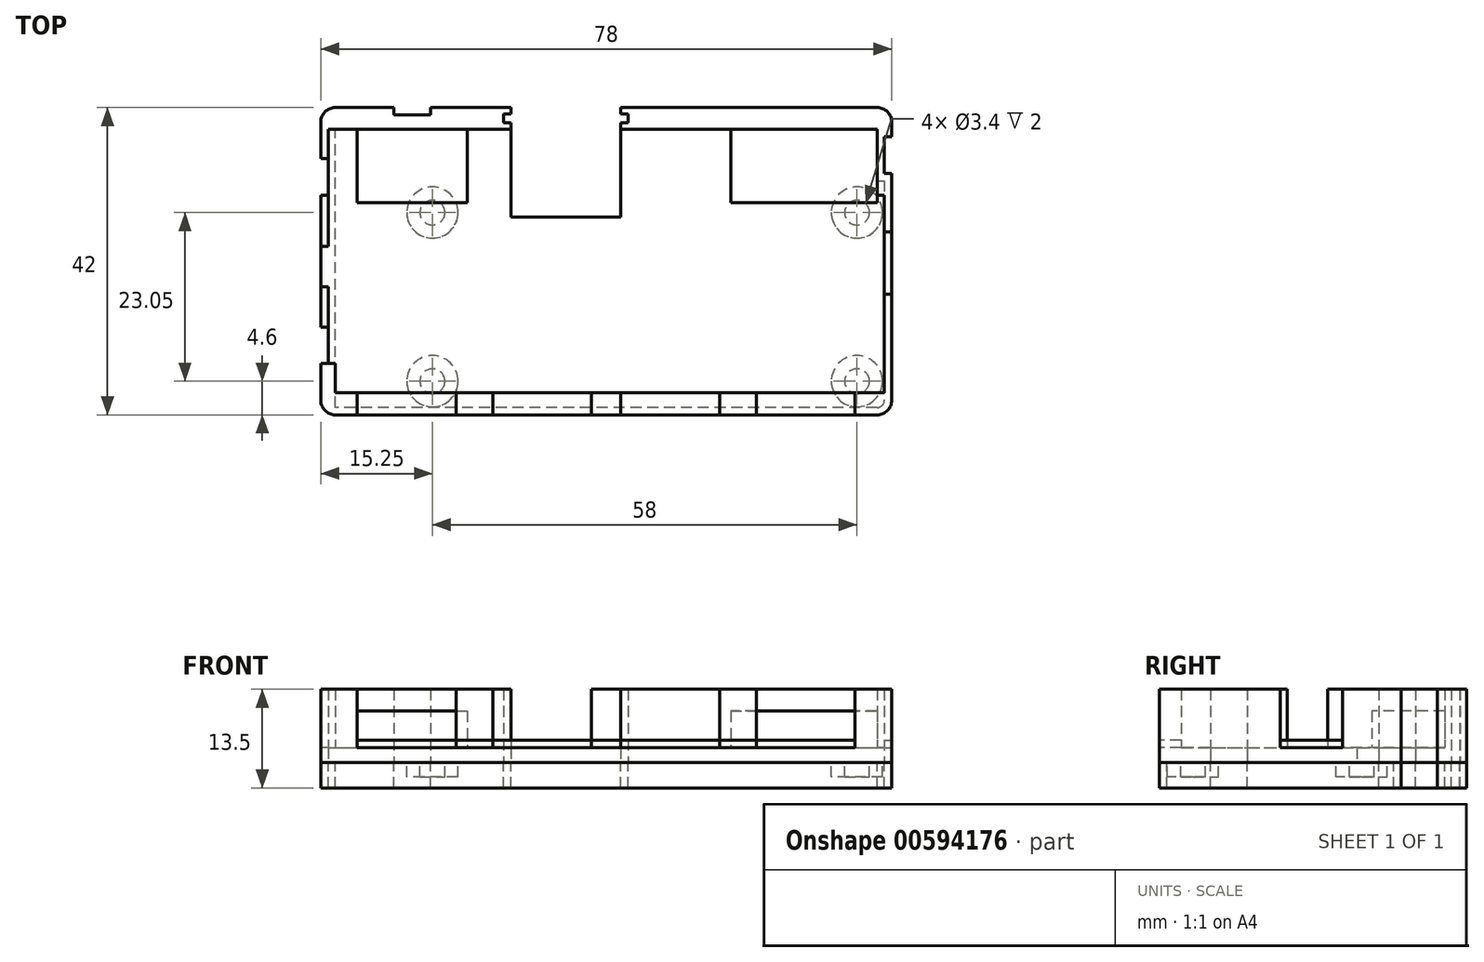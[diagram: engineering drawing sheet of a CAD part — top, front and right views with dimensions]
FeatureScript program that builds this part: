
annotation { "Feature Type Name" : "Feature", "Feature Type Description" : "" }
export const myFeature = defineFeature(function(context is Context, id is Id, definition is map)
    precondition{}
    {
        {
            var Q0;
            Q0=qCreatedBy(makeId("Top.planeOp"),FACE);
            var sketch = newSketch(context, id + "F0", { "sketchPlane" : qUnion([Q0])});
            skLineSegment(sketch, "E0", {"start": v(0, 0) * mm, "end": v(0, 7) * mm});
            skLineSegment(sketch, "E1", {"start": v(0, 7) * mm, "end": v(1, 7) * mm});
            skLineSegment(sketch, "E2", {"start": v(1, 7) * mm, "end": v(1, 12) * mm});
            skLineSegment(sketch, "E3", {"start": v(1, 12) * mm, "end": v(0, 12) * mm});
            skLineSegment(sketch, "E4", {"start": v(0, 12) * mm, "end": v(0, 30) * mm});
            skLineSegment(sketch, "E5", {"start": v(0, 30) * mm, "end": v(1, 30) * mm});
            skLineSegment(sketch, "E6", {"start": v(1, 30) * mm, "end": v(1, 35) * mm});
            skLineSegment(sketch, "E7", {"start": v(1, 35) * mm, "end": v(0, 35) * mm});
            skLineSegment(sketch, "E8", {"start": v(0, 35) * mm, "end": v(0, 42) * mm});
            skLineSegment(sketch, "E9", {"start": v(0, 42) * mm, "end": v(10, 42) * mm});
            skLineSegment(sketch, "E10", {"start": v(10, 42) * mm, "end": v(10, 41) * mm});
            skLineSegment(sketch, "E11", {"start": v(10, 41) * mm, "end": v(15, 41) * mm});
            skLineSegment(sketch, "E12", {"start": v(15, 41) * mm, "end": v(15, 42) * mm});
            skLineSegment(sketch, "E13", {"start": v(15, 42) * mm, "end": v(26, 42) * mm});
            skLineSegment(sketch, "E14", {"start": v(26, 42) * mm, "end": v(26, 41.1) * mm});
            skLineSegment(sketch, "E15", {"start": v(26, 41.1) * mm, "end": v(25, 41.1) * mm});
            skLineSegment(sketch, "E16", {"start": v(25, 41.1) * mm, "end": v(25, 39.9) * mm});
            skLineSegment(sketch, "E17", {"start": v(25, 39.9) * mm, "end": v(26, 39.9) * mm});
            skLineSegment(sketch, "E18", {"start": v(26, 39.9) * mm, "end": v(26, 27) * mm});
            skLineSegment(sketch, "E19", {"start": v(26, 27) * mm, "end": v(41, 27) * mm});
            skLineSegment(sketch, "E20", {"start": v(41, 27) * mm, "end": v(41, 39.9) * mm});
            skLineSegment(sketch, "E21", {"start": v(41, 39.9) * mm, "end": v(42, 39.9) * mm});
            skLineSegment(sketch, "E22", {"start": v(42, 39.9) * mm, "end": v(42, 41.1) * mm});
            skLineSegment(sketch, "E23", {"start": v(42, 41.1) * mm, "end": v(41, 41.1) * mm});
            skLineSegment(sketch, "E24", {"start": v(41, 41.1) * mm, "end": v(41, 42) * mm});
            skLineSegment(sketch, "E25", {"start": v(41, 42) * mm, "end": v(78, 42) * mm});
            skLineSegment(sketch, "E26", {"start": v(78, 42) * mm, "end": v(78, 38) * mm});
            skLineSegment(sketch, "E27", {"start": v(78, 38) * mm, "end": v(77, 38) * mm});
            skLineSegment(sketch, "E28", {"start": v(77, 38) * mm, "end": v(77, 33) * mm});
            skLineSegment(sketch, "E29", {"start": v(77, 33) * mm, "end": v(78, 33) * mm});
            skLineSegment(sketch, "E30", {"start": v(78, 33) * mm, "end": v(78, 0) * mm});
            skLineSegment(sketch, "E31", {"start": v(78, 0) * mm, "end": v(0, 0) * mm});
            skSolve(sketch);
        }
        {
            var Q0;
            Q0 = qSketchRegion(id + "F0", true);
            extrude(context, id + "F1", {"entities" : qUnion([Q0]), "depth" : 2 * mm, "offsetDistance" : 25 * mm});
        }
        {
            var Q0;
            Q0=makeQuery(id+"F1.opExtrude","CAP_FACE",FACE,{"disambiguationData":[OSD([sQuery(id+"F0.wireOp",EDGE,"E0"),sQuery(id+"F0.wireOp",EDGE,"E1"),sQuery(id+"F0.wireOp",EDGE,"E2"),sQuery(id+"F0.wireOp",EDGE,"E3"),sQuery(id+"F0.wireOp",EDGE,"E4"),sQuery(id+"F0.wireOp",EDGE,"E5"),sQuery(id+"F0.wireOp",EDGE,"E6"),sQuery(id+"F0.wireOp",EDGE,"E7"),sQuery(id+"F0.wireOp",EDGE,"E8"),sQuery(id+"F0.wireOp",EDGE,"E9"),sQuery(id+"F0.wireOp",EDGE,"E10"),sQuery(id+"F0.wireOp",EDGE,"E11"),sQuery(id+"F0.wireOp",EDGE,"E12"),sQuery(id+"F0.wireOp",EDGE,"E13"),sQuery(id+"F0.wireOp",EDGE,"E14"),sQuery(id+"F0.wireOp",EDGE,"E15"),sQuery(id+"F0.wireOp",EDGE,"E16"),sQuery(id+"F0.wireOp",EDGE,"E17"),sQuery(id+"F0.wireOp",EDGE,"E18"),sQuery(id+"F0.wireOp",EDGE,"E19"),sQuery(id+"F0.wireOp",EDGE,"E20"),sQuery(id+"F0.wireOp",EDGE,"E21"),sQuery(id+"F0.wireOp",EDGE,"E22"),sQuery(id+"F0.wireOp",EDGE,"E23"),sQuery(id+"F0.wireOp",EDGE,"E24"),sQuery(id+"F0.wireOp",EDGE,"E25"),sQuery(id+"F0.wireOp",EDGE,"E26"),sQuery(id+"F0.wireOp",EDGE,"E27"),sQuery(id+"F0.wireOp",EDGE,"E28"),sQuery(id+"F0.wireOp",EDGE,"E29"),sQuery(id+"F0.wireOp",EDGE,"E30"),sQuery(id+"F0.wireOp",EDGE,"E31")])],"isStart":false});
            var sketch = newSketch(context, id + "F2", { "sketchPlane" : qUnion([Q0])});
            skPoint(sketch, "E32.0", {"position": v(0, 0) * mm});
            skPoint(sketch, "E33.0", {"position": v(78, 0) * mm});
            skPoint(sketch, "E34.0", {"position": v(78, 42) * mm});
            skPoint(sketch, "E35.0", {"position": v(0, 42) * mm});
            skPoint(sketch, "E36.0", {"position": v(26, 42) * mm});
            skPoint(sketch, "E37.0", {"position": v(41, 42) * mm});
            skPoint(sketch, "E38.0", {"position": v(10, 42) * mm});
            skPoint(sketch, "E39.0", {"position": v(15, 42) * mm});
            skPoint(sketch, "E40.0", {"position": v(15, 41) * mm});
            skPoint(sketch, "E41.0", {"position": v(10, 41) * mm});
            skPoint(sketch, "E42.0", {"position": v(0, 35) * mm});
            skPoint(sketch, "E43.0", {"position": v(0, 7) * mm});
            skPoint(sketch, "E44.0", {"position": v(78, 38) * mm});
            skPoint(sketch, "E45.0", {"position": v(77, 38) * mm});
            skPoint(sketch, "E46.0", {"position": v(77, 33) * mm});
            skPoint(sketch, "E47.0", {"position": v(78, 33) * mm});
            skPoint(sketch, "E48.0", {"position": v(26, 41.1) * mm});
            skPoint(sketch, "E49.0", {"position": v(25, 41.1) * mm});
            skPoint(sketch, "E50.0", {"position": v(25, 39.9) * mm});
            skPoint(sketch, "E51.0", {"position": v(26, 39.9) * mm});
            skPoint(sketch, "E52.0", {"position": v(41, 41.1) * mm});
            skPoint(sketch, "E53.0", {"position": v(42, 41.1) * mm});
            skPoint(sketch, "E54.0", {"position": v(42, 39.9) * mm});
            skPoint(sketch, "E55.0", {"position": v(41, 39.9) * mm});
            skLineSegment(sketch, "E56", {"start": v(15, 42) * mm, "end": v(15, 41) * mm});
            skLineSegment(sketch, "E57", {"start": v(15, 41) * mm, "end": v(10, 41) * mm});
            skLineSegment(sketch, "E58", {"start": v(10, 42) * mm, "end": v(10, 41) * mm});
            skLineSegment(sketch, "E59", {"start": v(10, 42) * mm, "end": v(0, 42) * mm});
            skLineSegment(sketch, "E60", {"start": v(0, 42) * mm, "end": v(0, 35) * mm});
            skLineSegment(sketch, "E61", {"start": v(0, 35) * mm, "end": v(1, 35) * mm});
            skLineSegment(sketch, "E62", {"start": v(1, 35) * mm, "end": v(1, 39) * mm});
            skLineSegment(sketch, "E63", {"start": v(1, 39) * mm, "end": v(26, 39) * mm});
            skLineSegment(sketch, "E64", {"start": v(26, 39) * mm, "end": v(26, 39.9) * mm});
            skLineSegment(sketch, "E65", {"start": v(25, 39.9) * mm, "end": v(25, 41.1) * mm});
            skLineSegment(sketch, "E66", {"start": v(26, 41.1) * mm, "end": v(26, 42) * mm});
            skLineSegment(sketch, "E67", {"start": v(25, 41.1) * mm, "end": v(26, 41.1) * mm});
            skLineSegment(sketch, "E68", {"start": v(25, 39.9) * mm, "end": v(26, 39.9) * mm});
            skLineSegment(sketch, "E69", {"start": v(0, 30) * mm, "end": v(1, 30) * mm});
            skLineSegment(sketch, "E70", {"start": v(1, 30) * mm, "end": v(1, 23) * mm});
            skLineSegment(sketch, "E71", {"start": v(1, 23) * mm, "end": v(0, 23) * mm});
            skLineSegment(sketch, "E72", {"start": v(0, 23) * mm, "end": v(0, 30) * mm});
            skLineSegment(sketch, "E73", {"start": v(0, 12) * mm, "end": v(1, 12) * mm});
            skLineSegment(sketch, "E74", {"start": v(1, 12) * mm, "end": v(1, 17.5) * mm});
            skLineSegment(sketch, "E75", {"start": v(1, 17.5) * mm, "end": v(0, 17.5) * mm});
            skLineSegment(sketch, "E76", {"start": v(0, 17.5) * mm, "end": v(0, 12) * mm});
            skLineSegment(sketch, "E77", {"start": v(0, 7) * mm, "end": v(2, 7) * mm});
            skLineSegment(sketch, "E78", {"start": v(2, 7) * mm, "end": v(2, 3) * mm});
            skLineSegment(sketch, "E79", {"start": v(2, 3) * mm, "end": v(5, 3) * mm});
            skLineSegment(sketch, "E80", {"start": v(5, 3) * mm, "end": v(5, 0) * mm});
            skLineSegment(sketch, "E81", {"start": v(5, 0) * mm, "end": v(0, 0) * mm});
            skLineSegment(sketch, "E82", {"start": v(0, 7) * mm, "end": v(0, 0) * mm});
            skLineSegment(sketch, "E83", {"start": v(41, 39) * mm, "end": v(41, 39.9) * mm});
            skLineSegment(sketch, "E84", {"start": v(42, 39.9) * mm, "end": v(42, 41.1) * mm});
            skLineSegment(sketch, "E85", {"start": v(41, 41.1) * mm, "end": v(42, 41.1) * mm});
            skLineSegment(sketch, "E86", {"start": v(42, 39.9) * mm, "end": v(41, 39.9) * mm});
            skLineSegment(sketch, "E87", {"start": v(41, 41.1) * mm, "end": v(41, 42) * mm});
            skLineSegment(sketch, "E88", {"start": v(78, 42) * mm, "end": v(41, 42) * mm});
            skLineSegment(sketch, "E89", {"start": v(78, 42) * mm, "end": v(78, 38) * mm});
            skLineSegment(sketch, "E90", {"start": v(78, 38) * mm, "end": v(77, 38) * mm});
            skLineSegment(sketch, "E91", {"start": v(77, 38) * mm, "end": v(77, 33) * mm});
            skLineSegment(sketch, "E92", {"start": v(77, 33) * mm, "end": v(78, 33) * mm});
            skLineSegment(sketch, "E93", {"start": v(78, 33) * mm, "end": v(78, 25) * mm});
            skLineSegment(sketch, "E94", {"start": v(78, 25) * mm, "end": v(77, 25) * mm});
            skLineSegment(sketch, "E95", {"start": v(77, 25) * mm, "end": v(77, 30) * mm});
            skLineSegment(sketch, "E96", {"start": v(77, 30) * mm, "end": v(76, 30) * mm});
            skLineSegment(sketch, "E97", {"start": v(76, 30) * mm, "end": v(76, 39) * mm});
            skLineSegment(sketch, "E98", {"start": v(41, 39) * mm, "end": v(76, 39) * mm});
            skLineSegment(sketch, "E99", {"start": v(78, 16.5) * mm, "end": v(78, 0) * mm});
            skLineSegment(sketch, "E100", {"start": v(78, 0) * mm, "end": v(73, 0) * mm});
            skLineSegment(sketch, "E101", {"start": v(73, 0) * mm, "end": v(73, 3) * mm});
            skLineSegment(sketch, "E102", {"start": v(73, 3) * mm, "end": v(77, 3) * mm});
            skLineSegment(sketch, "E103", {"start": v(77, 3) * mm, "end": v(77, 16.5) * mm});
            skLineSegment(sketch, "E104", {"start": v(77, 16.5) * mm, "end": v(78, 16.5) * mm});
            skLineSegment(sketch, "E105.bottom", {"start": v(18.5, 0) * mm, "end": v(23.5, 0) * mm});
            skLineSegment(sketch, "E105.top", {"start": v(18.5, 3) * mm, "end": v(23.5, 3) * mm});
            skLineSegment(sketch, "E105.left", {"start": v(18.5, 0) * mm, "end": v(18.5, 3) * mm});
            skLineSegment(sketch, "E105.right", {"start": v(23.5, 0) * mm, "end": v(23.5, 3) * mm});
            skLineSegment(sketch, "E106.bottom", {"start": v(37, 3) * mm, "end": v(41, 3) * mm});
            skLineSegment(sketch, "E106.top", {"start": v(37, 0) * mm, "end": v(41, 0) * mm});
            skLineSegment(sketch, "E106.left", {"start": v(37, 3) * mm, "end": v(37, 0) * mm});
            skLineSegment(sketch, "E106.right", {"start": v(41, 3) * mm, "end": v(41, 0) * mm});
            skLineSegment(sketch, "E107.bottom", {"start": v(54.5, 3) * mm, "end": v(59.5, 3) * mm});
            skLineSegment(sketch, "E107.top", {"start": v(54.5, 0) * mm, "end": v(59.5, 0) * mm});
            skLineSegment(sketch, "E107.left", {"start": v(54.5, 3) * mm, "end": v(54.5, 0) * mm});
            skLineSegment(sketch, "E107.right", {"start": v(59.5, 3) * mm, "end": v(59.5, 0) * mm});
            skLineSegment(sketch, "E108", {"start": v(15, 42) * mm, "end": v(26, 42) * mm});
            skSolve(sketch);
        }
        {
            var Q0;
            Q0 = qSketchRegion(id + "F2", true);
            extrude(context, id + "F3", {"entities" : qUnion([Q0]), "operationType" : NewBodyOperationType.ADD, "depth" : 8 * mm, "offsetDistance" : 25 * mm});
        }
        {
            var Q0;
            Q0=makeQuery(id+"F1.opExtrude","CAP_FACE",FACE,{"disambiguationData":[OSD([sQuery(id+"F0.wireOp",EDGE,"E0"),sQuery(id+"F0.wireOp",EDGE,"E1"),sQuery(id+"F0.wireOp",EDGE,"E2"),sQuery(id+"F0.wireOp",EDGE,"E3"),sQuery(id+"F0.wireOp",EDGE,"E4"),sQuery(id+"F0.wireOp",EDGE,"E5"),sQuery(id+"F0.wireOp",EDGE,"E6"),sQuery(id+"F0.wireOp",EDGE,"E7"),sQuery(id+"F0.wireOp",EDGE,"E8"),sQuery(id+"F0.wireOp",EDGE,"E9"),sQuery(id+"F0.wireOp",EDGE,"E10"),sQuery(id+"F0.wireOp",EDGE,"E11"),sQuery(id+"F0.wireOp",EDGE,"E12"),sQuery(id+"F0.wireOp",EDGE,"E13"),sQuery(id+"F0.wireOp",EDGE,"E14"),sQuery(id+"F0.wireOp",EDGE,"E15"),sQuery(id+"F0.wireOp",EDGE,"E16"),sQuery(id+"F0.wireOp",EDGE,"E17"),sQuery(id+"F0.wireOp",EDGE,"E18"),sQuery(id+"F0.wireOp",EDGE,"E19"),sQuery(id+"F0.wireOp",EDGE,"E20"),sQuery(id+"F0.wireOp",EDGE,"E21"),sQuery(id+"F0.wireOp",EDGE,"E22"),sQuery(id+"F0.wireOp",EDGE,"E23"),sQuery(id+"F0.wireOp",EDGE,"E24"),sQuery(id+"F0.wireOp",EDGE,"E25"),sQuery(id+"F0.wireOp",EDGE,"E26"),sQuery(id+"F0.wireOp",EDGE,"E27"),sQuery(id+"F0.wireOp",EDGE,"E28"),sQuery(id+"F0.wireOp",EDGE,"E29"),sQuery(id+"F0.wireOp",EDGE,"E30"),sQuery(id+"F0.wireOp",EDGE,"E31")])],"isStart":false});
            var sketch = newSketch(context, id + "F4", { "sketchPlane" : qUnion([Q0])});
            skPoint(sketch, "E109.0", {"position": v(5, 0) * mm});
            skPoint(sketch, "E110.0", {"position": v(73, 3) * mm});
            skPoint(sketch, "E111.0", {"position": v(78, 16.5) * mm});
            skPoint(sketch, "E112.0", {"position": v(77, 25) * mm});
            skLineSegment(sketch, "E113.bottom", {"start": v(5, 0) * mm, "end": v(73, 0) * mm});
            skLineSegment(sketch, "E113.top", {"start": v(5, 3) * mm, "end": v(73, 3) * mm});
            skLineSegment(sketch, "E113.left", {"start": v(5, 0) * mm, "end": v(5, 3) * mm});
            skLineSegment(sketch, "E113.right", {"start": v(73, 0) * mm, "end": v(73, 3) * mm});
            skLineSegment(sketch, "E114.bottom", {"start": v(78, 16.5) * mm, "end": v(77, 16.5) * mm});
            skLineSegment(sketch, "E114.top", {"start": v(78, 25) * mm, "end": v(77, 25) * mm});
            skLineSegment(sketch, "E114.left", {"start": v(78, 16.5) * mm, "end": v(78, 25) * mm});
            skLineSegment(sketch, "E114.right", {"start": v(77, 16.5) * mm, "end": v(77, 25) * mm});
            skSolve(sketch);
        }
        {
            var Q0;
            Q0 = qSketchRegion(id + "F4", true);
            extrude(context, id + "F5", {"entities" : qUnion([Q0]), "depth" : 1 * mm, "offsetDistance" : 25 * mm});
        }
        {
            var Q0;
            Q0=makeQuery(id+"F1.opExtrude","CAP_FACE",FACE,{"disambiguationData":[OSD([sQuery(id+"F0.wireOp",EDGE,"E0"),sQuery(id+"F0.wireOp",EDGE,"E1"),sQuery(id+"F0.wireOp",EDGE,"E2"),sQuery(id+"F0.wireOp",EDGE,"E3"),sQuery(id+"F0.wireOp",EDGE,"E4"),sQuery(id+"F0.wireOp",EDGE,"E5"),sQuery(id+"F0.wireOp",EDGE,"E6"),sQuery(id+"F0.wireOp",EDGE,"E7"),sQuery(id+"F0.wireOp",EDGE,"E8"),sQuery(id+"F0.wireOp",EDGE,"E9"),sQuery(id+"F0.wireOp",EDGE,"E10"),sQuery(id+"F0.wireOp",EDGE,"E11"),sQuery(id+"F0.wireOp",EDGE,"E12"),sQuery(id+"F0.wireOp",EDGE,"E13"),sQuery(id+"F0.wireOp",EDGE,"E14"),sQuery(id+"F0.wireOp",EDGE,"E15"),sQuery(id+"F0.wireOp",EDGE,"E16"),sQuery(id+"F0.wireOp",EDGE,"E17"),sQuery(id+"F0.wireOp",EDGE,"E18"),sQuery(id+"F0.wireOp",EDGE,"E19"),sQuery(id+"F0.wireOp",EDGE,"E20"),sQuery(id+"F0.wireOp",EDGE,"E21"),sQuery(id+"F0.wireOp",EDGE,"E22"),sQuery(id+"F0.wireOp",EDGE,"E23"),sQuery(id+"F0.wireOp",EDGE,"E24"),sQuery(id+"F0.wireOp",EDGE,"E25"),sQuery(id+"F0.wireOp",EDGE,"E26"),sQuery(id+"F0.wireOp",EDGE,"E27"),sQuery(id+"F0.wireOp",EDGE,"E28"),sQuery(id+"F0.wireOp",EDGE,"E29"),sQuery(id+"F0.wireOp",EDGE,"E30"),sQuery(id+"F0.wireOp",EDGE,"E31")])],"isStart":false});
            var sketch = newSketch(context, id + "F6", { "sketchPlane" : qUnion([Q0])});
            skPoint(sketch, "E115.0", {"position": v(1, 39) * mm});
            skPoint(sketch, "E116.0", {"position": v(76, 39) * mm});
            skLineSegment(sketch, "E117.bottom", {"start": v(5, 39) * mm, "end": v(20, 39) * mm});
            skLineSegment(sketch, "E117.top", {"start": v(5, 29) * mm, "end": v(20, 29) * mm});
            skLineSegment(sketch, "E117.left", {"start": v(5, 39) * mm, "end": v(5, 29) * mm});
            skLineSegment(sketch, "E117.right", {"start": v(20, 39) * mm, "end": v(20, 29) * mm});
            skLineSegment(sketch, "E118.bottom", {"start": v(76, 39) * mm, "end": v(56, 39) * mm});
            skLineSegment(sketch, "E118.top", {"start": v(76, 29) * mm, "end": v(56, 29) * mm});
            skLineSegment(sketch, "E118.left", {"start": v(76, 39) * mm, "end": v(76, 29) * mm});
            skLineSegment(sketch, "E118.right", {"start": v(56, 39) * mm, "end": v(56, 29) * mm});
            skSolve(sketch);
        }
        {
            var Q0;
            Q0 = qSketchRegion(id + "F6", true);
            extrude(context, id + "F7", {"entities" : qUnion([Q0]), "depth" : 5 * mm, "offsetDistance" : 25 * mm});
        }
        {
            var Q0;
            Q0=makeQuery(id+"F1.opExtrude","CAP_FACE",FACE,{"disambiguationData":[OSD([sQuery(id+"F0.wireOp",EDGE,"E0"),sQuery(id+"F0.wireOp",EDGE,"E1"),sQuery(id+"F0.wireOp",EDGE,"E2"),sQuery(id+"F0.wireOp",EDGE,"E3"),sQuery(id+"F0.wireOp",EDGE,"E4"),sQuery(id+"F0.wireOp",EDGE,"E5"),sQuery(id+"F0.wireOp",EDGE,"E6"),sQuery(id+"F0.wireOp",EDGE,"E7"),sQuery(id+"F0.wireOp",EDGE,"E8"),sQuery(id+"F0.wireOp",EDGE,"E9"),sQuery(id+"F0.wireOp",EDGE,"E10"),sQuery(id+"F0.wireOp",EDGE,"E11"),sQuery(id+"F0.wireOp",EDGE,"E12"),sQuery(id+"F0.wireOp",EDGE,"E13"),sQuery(id+"F0.wireOp",EDGE,"E14"),sQuery(id+"F0.wireOp",EDGE,"E15"),sQuery(id+"F0.wireOp",EDGE,"E16"),sQuery(id+"F0.wireOp",EDGE,"E17"),sQuery(id+"F0.wireOp",EDGE,"E18"),sQuery(id+"F0.wireOp",EDGE,"E19"),sQuery(id+"F0.wireOp",EDGE,"E20"),sQuery(id+"F0.wireOp",EDGE,"E21"),sQuery(id+"F0.wireOp",EDGE,"E22"),sQuery(id+"F0.wireOp",EDGE,"E23"),sQuery(id+"F0.wireOp",EDGE,"E24"),sQuery(id+"F0.wireOp",EDGE,"E25"),sQuery(id+"F0.wireOp",EDGE,"E26"),sQuery(id+"F0.wireOp",EDGE,"E27"),sQuery(id+"F0.wireOp",EDGE,"E28"),sQuery(id+"F0.wireOp",EDGE,"E29"),sQuery(id+"F0.wireOp",EDGE,"E30"),sQuery(id+"F0.wireOp",EDGE,"E31")])],"isStart":true});
            var sketch = newSketch(context, id + "F8", { "sketchPlane" : qUnion([Q0])});
            skPoint(sketch, "E119.0", {"position": v(0, 0) * mm});
            skPoint(sketch, "E120.0", {"position": v(1, -7) * mm});
            skPoint(sketch, "E121.0", {"position": v(0, -7) * mm});
            skPoint(sketch, "E122.0", {"position": v(1, -12) * mm});
            skPoint(sketch, "E123.0", {"position": v(0, -12) * mm});
            skPoint(sketch, "E124.0", {"position": v(0, -30) * mm});
            skPoint(sketch, "E125.0", {"position": v(1, -30) * mm});
            skPoint(sketch, "E126.0", {"position": v(1, -35) * mm});
            skPoint(sketch, "E127.0", {"position": v(0, -35) * mm});
            skPoint(sketch, "E128.0", {"position": v(0, -42) * mm});
            skPoint(sketch, "E129.0", {"position": v(10, -42) * mm});
            skPoint(sketch, "E130.0", {"position": v(10, -41) * mm});
            skPoint(sketch, "E131.0", {"position": v(15, -41) * mm});
            skPoint(sketch, "E132.0", {"position": v(15, -42) * mm});
            skPoint(sketch, "E133.0", {"position": v(26, -42) * mm});
            skPoint(sketch, "E134.0", {"position": v(26, -41.1) * mm});
            skPoint(sketch, "E135.0", {"position": v(25, -41.1) * mm});
            skPoint(sketch, "E136.0", {"position": v(25, -39.9) * mm});
            skPoint(sketch, "E137.0", {"position": v(26, -39.9) * mm});
            skPoint(sketch, "E138.0", {"position": v(41, -39.9) * mm});
            skPoint(sketch, "E139.0", {"position": v(42, -39.9) * mm});
            skPoint(sketch, "E140.0", {"position": v(42, -41.1) * mm});
            skPoint(sketch, "E141.0", {"position": v(41, -41.1) * mm});
            skPoint(sketch, "E142.0", {"position": v(41, -42) * mm});
            skPoint(sketch, "E143.0", {"position": v(78, -42) * mm});
            skPoint(sketch, "E144.0", {"position": v(78, -38) * mm});
            skPoint(sketch, "E145.0", {"position": v(77, -38) * mm});
            skPoint(sketch, "E146.0", {"position": v(77, -33) * mm});
            skPoint(sketch, "E147.0", {"position": v(78, -33) * mm});
            skPoint(sketch, "E148.0", {"position": v(78, 0) * mm});
            skLineSegment(sketch, "E149", {"start": v(0, 0) * mm, "end": v(78, 0) * mm});
            skLineSegment(sketch, "E150", {"start": v(78, 0) * mm, "end": v(78, -33) * mm});
            skLineSegment(sketch, "E151", {"start": v(78, -33) * mm, "end": v(77, -33) * mm});
            skLineSegment(sketch, "E152", {"start": v(77, -33) * mm, "end": v(77, -38) * mm});
            skLineSegment(sketch, "E153", {"start": v(77, -38) * mm, "end": v(78, -38) * mm});
            skLineSegment(sketch, "E154", {"start": v(78, -38) * mm, "end": v(78, -42) * mm});
            skLineSegment(sketch, "E155", {"start": v(78, -42) * mm, "end": v(41, -42) * mm});
            skLineSegment(sketch, "E156", {"start": v(41, -42) * mm, "end": v(41, -41.1) * mm});
            skLineSegment(sketch, "E157", {"start": v(41, -41.1) * mm, "end": v(42, -41.1) * mm});
            skLineSegment(sketch, "E158", {"start": v(41, -39.9) * mm, "end": v(41, -39) * mm});
            skLineSegment(sketch, "E159", {"start": v(41, -39) * mm, "end": v(76, -39) * mm});
            skLineSegment(sketch, "E160", {"start": v(76, -39) * mm, "end": v(76, -32) * mm});
            skLineSegment(sketch, "E161", {"start": v(76, -32) * mm, "end": v(77, -32) * mm});
            skLineSegment(sketch, "E162", {"start": v(77, -32) * mm, "end": v(77, -1) * mm});
            skLineSegment(sketch, "E163", {"start": v(77, -1) * mm, "end": v(2, -1) * mm});
            skLineSegment(sketch, "E164", {"start": v(2, -1) * mm, "end": v(2, -39) * mm});
            skLineSegment(sketch, "E165", {"start": v(2, -39) * mm, "end": v(26, -39) * mm});
            skLineSegment(sketch, "E166", {"start": v(26, -39) * mm, "end": v(26, -39.9) * mm});
            skLineSegment(sketch, "E167", {"start": v(26, -39.9) * mm, "end": v(25, -39.9) * mm});
            skLineSegment(sketch, "E168", {"start": v(25, -39.9) * mm, "end": v(25, -41.1) * mm});
            skLineSegment(sketch, "E169", {"start": v(25, -41.1) * mm, "end": v(26, -41.1) * mm});
            skLineSegment(sketch, "E170", {"start": v(26, -41.1) * mm, "end": v(26, -42) * mm});
            skLineSegment(sketch, "E171", {"start": v(26, -42) * mm, "end": v(15, -42) * mm});
            skLineSegment(sketch, "E172", {"start": v(15, -42) * mm, "end": v(15, -41) * mm});
            skLineSegment(sketch, "E173", {"start": v(15, -41) * mm, "end": v(10, -41) * mm});
            skLineSegment(sketch, "E174", {"start": v(10, -42) * mm, "end": v(10, -41) * mm});
            skLineSegment(sketch, "E175", {"start": v(10, -42) * mm, "end": v(0, -42) * mm});
            skLineSegment(sketch, "E176", {"start": v(0, -42) * mm, "end": v(0, -35) * mm});
            skLineSegment(sketch, "E177", {"start": v(0, -35) * mm, "end": v(1, -35) * mm});
            skLineSegment(sketch, "E178", {"start": v(1, -35) * mm, "end": v(1, -30) * mm});
            skLineSegment(sketch, "E179", {"start": v(1, -30) * mm, "end": v(0, -30) * mm});
            skLineSegment(sketch, "E180", {"start": v(0, -30) * mm, "end": v(0, -12) * mm});
            skLineSegment(sketch, "E181", {"start": v(0, -12) * mm, "end": v(1, -12) * mm});
            skLineSegment(sketch, "E182", {"start": v(1, -12) * mm, "end": v(1, -7) * mm});
            skLineSegment(sketch, "E183", {"start": v(1, -7) * mm, "end": v(0, -7) * mm});
            skLineSegment(sketch, "E184", {"start": v(0, -7) * mm, "end": v(0, 0) * mm});
            skLineSegment(sketch, "E185", {"start": v(42, -39.9) * mm, "end": v(41, -39.9) * mm});
            skLineSegment(sketch, "E186", {"start": v(42, -39.9) * mm, "end": v(42, -41.1) * mm});
            skSolve(sketch);
        }
        {
            var Q0;
            Q0 = qSketchRegion(id + "F8", true);
            extrude(context, id + "F9", {"entities" : qUnion([Q0]), "depth" : 3.5 * mm, "offsetDistance" : 25 * mm});
        }
        {
            var Q0;
            Q0=makeQuery(id+"F1.opExtrude","CAP_FACE",FACE,{"disambiguationData":[OSD([sQuery(id+"F0.wireOp",EDGE,"E0"),sQuery(id+"F0.wireOp",EDGE,"E1"),sQuery(id+"F0.wireOp",EDGE,"E2"),sQuery(id+"F0.wireOp",EDGE,"E3"),sQuery(id+"F0.wireOp",EDGE,"E4"),sQuery(id+"F0.wireOp",EDGE,"E5"),sQuery(id+"F0.wireOp",EDGE,"E6"),sQuery(id+"F0.wireOp",EDGE,"E7"),sQuery(id+"F0.wireOp",EDGE,"E8"),sQuery(id+"F0.wireOp",EDGE,"E9"),sQuery(id+"F0.wireOp",EDGE,"E10"),sQuery(id+"F0.wireOp",EDGE,"E11"),sQuery(id+"F0.wireOp",EDGE,"E12"),sQuery(id+"F0.wireOp",EDGE,"E13"),sQuery(id+"F0.wireOp",EDGE,"E14"),sQuery(id+"F0.wireOp",EDGE,"E15"),sQuery(id+"F0.wireOp",EDGE,"E16"),sQuery(id+"F0.wireOp",EDGE,"E17"),sQuery(id+"F0.wireOp",EDGE,"E18"),sQuery(id+"F0.wireOp",EDGE,"E19"),sQuery(id+"F0.wireOp",EDGE,"E20"),sQuery(id+"F0.wireOp",EDGE,"E21"),sQuery(id+"F0.wireOp",EDGE,"E22"),sQuery(id+"F0.wireOp",EDGE,"E23"),sQuery(id+"F0.wireOp",EDGE,"E24"),sQuery(id+"F0.wireOp",EDGE,"E25"),sQuery(id+"F0.wireOp",EDGE,"E26"),sQuery(id+"F0.wireOp",EDGE,"E27"),sQuery(id+"F0.wireOp",EDGE,"E28"),sQuery(id+"F0.wireOp",EDGE,"E29"),sQuery(id+"F0.wireOp",EDGE,"E30"),sQuery(id+"F0.wireOp",EDGE,"E31")])],"isStart":true});
            var sketch = newSketch(context, id + "F10", { "sketchPlane" : qUnion([Q0])});
            skPoint(sketch, "E187.0", {"position": v(78, 0) * mm});
            skCircle(sketch, "E188", {"center": v(73.25, -4.6) * mm, "radius": 3.5 * mm});
            skCircle(sketch, "E189", {"center": v(73.25, -4.6) * mm, "radius": 1.7 * mm});
            skCircle(sketch, "E190.0.1.0", {"center": v(73.25, -27.65) * mm, "radius": 1.7 * mm});
            skCircle(sketch, "E190.0.1.1", {"center": v(73.25, -27.65) * mm, "radius": 3.5 * mm});
            skCircle(sketch, "E190.1.0.0", {"center": v(15.25, -4.6) * mm, "radius": 1.7 * mm});
            skCircle(sketch, "E190.1.0.1", {"center": v(15.25, -4.6) * mm, "radius": 3.5 * mm});
            skCircle(sketch, "E190.1.1.0", {"center": v(15.25, -27.65) * mm, "radius": 1.7 * mm});
            skCircle(sketch, "E190.1.1.1", {"center": v(15.25, -27.65) * mm, "radius": 3.5 * mm});
            skLineSegment(sketch, "E190.direction1", {"start": v(73.25, -4.6) * mm, "end": v(15.25, -4.6) * mm, "construction": true});
            skLineSegment(sketch, "E190.direction2", {"start": v(73.25, -4.6) * mm, "end": v(73.25, -27.65) * mm, "construction": true});
            skSolve(sketch);
        }
        {
            var Q0;
            Q0 = qSketchRegion(id + "F10", true);
            extrude(context, id + "F11", {"entities" : qUnion([Q0]), "operationType" : NewBodyOperationType.ADD, "depth" : 2 * mm, "offsetDistance" : 25 * mm});
        }
        {
            var Q0;
            Q0=makeQuery(id+"F5.opExtrude","SWEPT_BODY",BODY,{"disambiguationData":[OSD([sQuery(id+"F4.wireOp",EDGE,"E114.bottom"),sQuery(id+"F4.wireOp",EDGE,"E114.top"),sQuery(id+"F4.wireOp",EDGE,"E114.left"),sQuery(id+"F4.wireOp",EDGE,"E114.right")])]});
            var Q1;
            Q1=makeQuery(id+"F9.opExtrude","SWEPT_BODY",BODY,{"disambiguationData":[OSD([sQuery(id+"F8.wireOp",EDGE,"E149"),sQuery(id+"F8.wireOp",EDGE,"E150"),sQuery(id+"F8.wireOp",EDGE,"E151"),sQuery(id+"F8.wireOp",EDGE,"E152"),sQuery(id+"F8.wireOp",EDGE,"E153"),sQuery(id+"F8.wireOp",EDGE,"E154"),sQuery(id+"F8.wireOp",EDGE,"E155"),sQuery(id+"F8.wireOp",EDGE,"E156"),sQuery(id+"F8.wireOp",EDGE,"E157"),sQuery(id+"F8.wireOp",EDGE,"E158"),sQuery(id+"F8.wireOp",EDGE,"E159"),sQuery(id+"F8.wireOp",EDGE,"E160"),sQuery(id+"F8.wireOp",EDGE,"E161"),sQuery(id+"F8.wireOp",EDGE,"E162"),sQuery(id+"F8.wireOp",EDGE,"E163"),sQuery(id+"F8.wireOp",EDGE,"E164"),sQuery(id+"F8.wireOp",EDGE,"E165"),sQuery(id+"F8.wireOp",EDGE,"E166"),sQuery(id+"F8.wireOp",EDGE,"E167"),sQuery(id+"F8.wireOp",EDGE,"E168"),sQuery(id+"F8.wireOp",EDGE,"E169"),sQuery(id+"F8.wireOp",EDGE,"E170"),sQuery(id+"F8.wireOp",EDGE,"E171"),sQuery(id+"F8.wireOp",EDGE,"E172"),sQuery(id+"F8.wireOp",EDGE,"E173"),sQuery(id+"F8.wireOp",EDGE,"E174"),sQuery(id+"F8.wireOp",EDGE,"E175"),sQuery(id+"F8.wireOp",EDGE,"E176"),sQuery(id+"F8.wireOp",EDGE,"E177"),sQuery(id+"F8.wireOp",EDGE,"E178"),sQuery(id+"F8.wireOp",EDGE,"E179"),sQuery(id+"F8.wireOp",EDGE,"E180"),sQuery(id+"F8.wireOp",EDGE,"E181"),sQuery(id+"F8.wireOp",EDGE,"E182"),sQuery(id+"F8.wireOp",EDGE,"E183"),sQuery(id+"F8.wireOp",EDGE,"E184"),sQuery(id+"F8.wireOp",EDGE,"E185"),sQuery(id+"F8.wireOp",EDGE,"E186")])]});
            booleanBodies(context, id + "F12", {"operationType" : BooleanOperationType.UNION, "tools" : qUnion([Q0, Q1])});
        }
        {
            var Q0;
            Q0=makeQuery(id+"F12.opBoolean","MERGE",EDGE,{"derivedFrom":[makeQuery(id+"F3.boolean.opBoolean","MERGE",EDGE,{"derivedFrom":[makeQuery(id+"F1.opExtrude","SWEPT_EDGE",EDGE,{"disambiguationData":[OSD([sQuery(id+"F0.wireOp",EDGE,"E30"),sQuery(id+"F0.wireOp",EDGE,"E31")])]}),makeQuery(id+"F3.opExtrude","SWEPT_EDGE",EDGE,{"disambiguationData":[OSD([sQuery(id+"F2.wireOp",EDGE,"E99"),sQuery(id+"F2.wireOp",EDGE,"E100")])]})]}),makeQuery(id+"F9.opExtrude","SWEPT_EDGE",EDGE,{"disambiguationData":[OSD([sQuery(id+"F8.wireOp",EDGE,"E149"),sQuery(id+"F8.wireOp",EDGE,"E150")])]})]});
            var Q1;
            Q1=makeQuery(id+"F12.opBoolean","MERGE",EDGE,{"derivedFrom":[makeQuery(id+"F3.boolean.opBoolean","MERGE",EDGE,{"derivedFrom":[makeQuery(id+"F1.opExtrude","SWEPT_EDGE",EDGE,{"disambiguationData":[OSD([sQuery(id+"F0.wireOp",EDGE,"E25"),sQuery(id+"F0.wireOp",EDGE,"E26")])]}),makeQuery(id+"F3.opExtrude","SWEPT_EDGE",EDGE,{"disambiguationData":[OSD([sQuery(id+"F2.wireOp",EDGE,"E88"),sQuery(id+"F2.wireOp",EDGE,"E89")])]})]}),makeQuery(id+"F9.opExtrude","SWEPT_EDGE",EDGE,{"disambiguationData":[OSD([sQuery(id+"F8.wireOp",EDGE,"E154"),sQuery(id+"F8.wireOp",EDGE,"E155")])]})]});
            var Q2;
            Q2=makeQuery(id+"F12.opBoolean","MERGE",EDGE,{"derivedFrom":[makeQuery(id+"F3.boolean.opBoolean","MERGE",EDGE,{"derivedFrom":[makeQuery(id+"F1.opExtrude","SWEPT_EDGE",EDGE,{"disambiguationData":[OSD([sQuery(id+"F0.wireOp",EDGE,"E0"),sQuery(id+"F0.wireOp",EDGE,"E31")])]}),makeQuery(id+"F3.opExtrude","SWEPT_EDGE",EDGE,{"disambiguationData":[OSD([sQuery(id+"F2.wireOp",EDGE,"E81"),sQuery(id+"F2.wireOp",EDGE,"E82")])]})]}),makeQuery(id+"F9.opExtrude","SWEPT_EDGE",EDGE,{"disambiguationData":[OSD([sQuery(id+"F8.wireOp",EDGE,"E149"),sQuery(id+"F8.wireOp",EDGE,"E184")])]})]});
            var Q3;
            Q3=makeQuery(id+"F12.opBoolean","MERGE",EDGE,{"derivedFrom":[makeQuery(id+"F3.boolean.opBoolean","MERGE",EDGE,{"derivedFrom":[makeQuery(id+"F1.opExtrude","SWEPT_EDGE",EDGE,{"disambiguationData":[OSD([sQuery(id+"F0.wireOp",EDGE,"E8"),sQuery(id+"F0.wireOp",EDGE,"E9")])]}),makeQuery(id+"F3.opExtrude","SWEPT_EDGE",EDGE,{"disambiguationData":[OSD([sQuery(id+"F2.wireOp",EDGE,"E59"),sQuery(id+"F2.wireOp",EDGE,"E60")])]})]}),makeQuery(id+"F9.opExtrude","SWEPT_EDGE",EDGE,{"disambiguationData":[OSD([sQuery(id+"F8.wireOp",EDGE,"E175"),sQuery(id+"F8.wireOp",EDGE,"E176")])]})]});
            fillet(context, id + "F13", {"entities" : qUnion([Q0, Q1, Q2, Q3]), "radius" : 2 * mm, "tangentPropagation" : true, "allowEdgeOverflow" : false});
        }
        {
            var Q0;
            Q0=makeQuery(id+"F9.opExtrude","SWEPT_EDGE",EDGE,{"disambiguationData":[OSD([sQuery(id+"F8.wireOp",EDGE,"E162"),sQuery(id+"F8.wireOp",EDGE,"E163")])]});
            fillet(context, id + "F14", {"entities" : qUnion([Q0]), "radius" : 1 * mm, "tangentPropagation" : true, "allowEdgeOverflow" : false});
        }
    });
